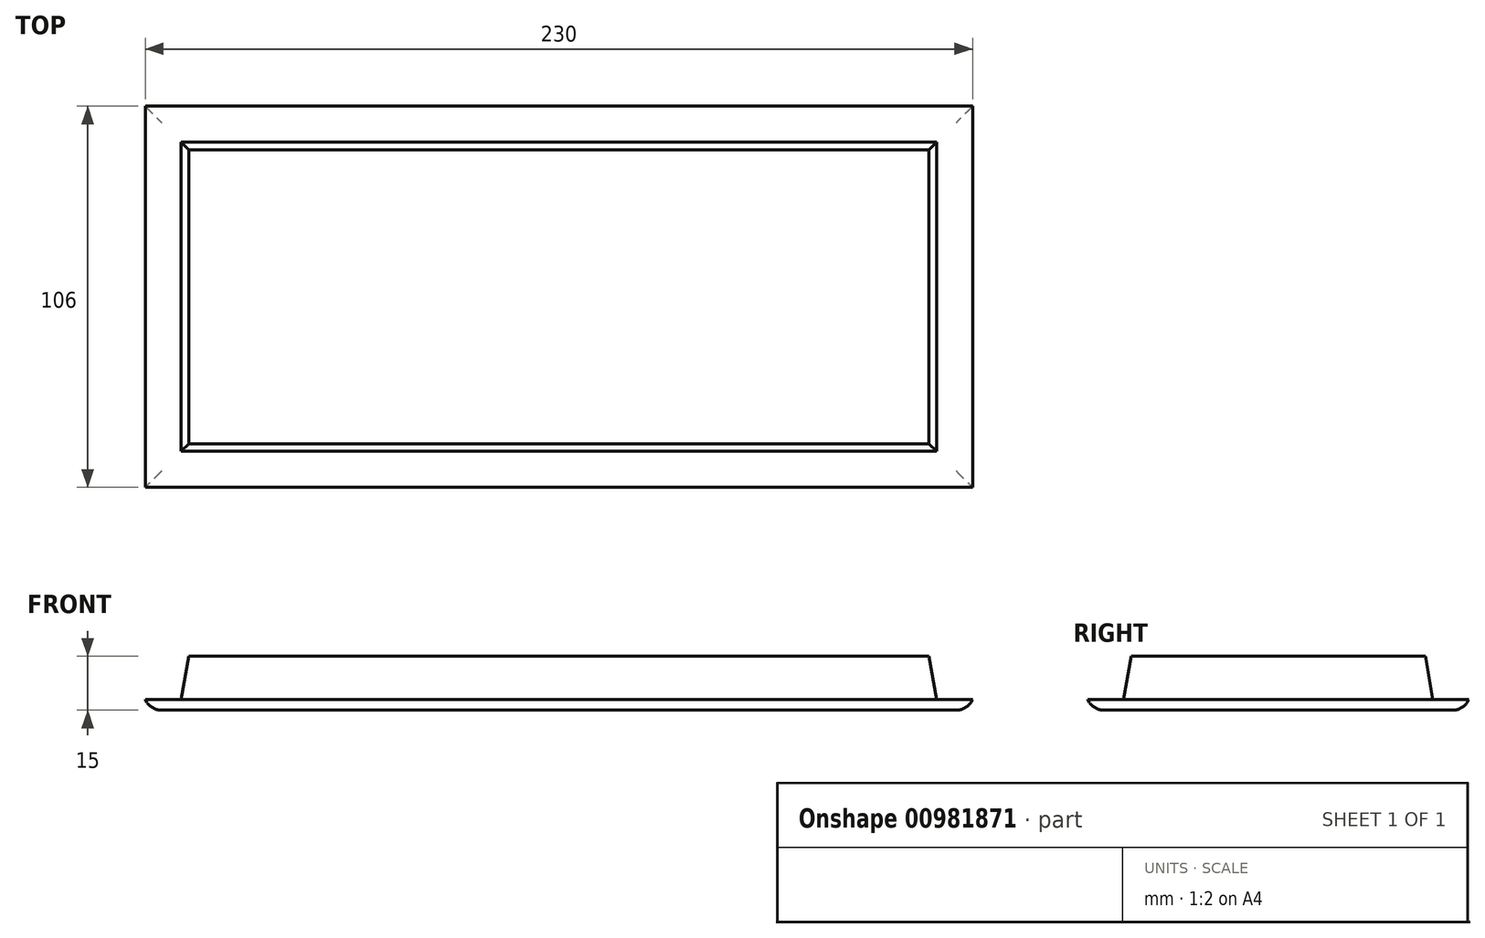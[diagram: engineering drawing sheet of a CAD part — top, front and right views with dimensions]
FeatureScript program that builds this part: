
annotation { "Feature Type Name" : "Feature", "Feature Type Description" : "" }
export const myFeature = defineFeature(function(context is Context, id is Id, definition is map)
    precondition{}
    {
        {
            var Q0;
            Q0=qCreatedBy(makeId("Top.planeOp"),FACE);
            var sketch = newSketch(context, id + "F0", { "sketchPlane" : qUnion([Q0])});
            skLineSegment(sketch, "E0.bottom", {"start": v(105, -43) * mm, "end": v(-105, -43) * mm});
            skLineSegment(sketch, "E0.top", {"start": v(105, 43) * mm, "end": v(-105, 43) * mm});
            skLineSegment(sketch, "E0.left", {"start": v(105, -43) * mm, "end": v(105, 43) * mm});
            skLineSegment(sketch, "E0.right", {"start": v(-105, -43) * mm, "end": v(-105, 43) * mm});
            skPoint(sketch, "E0.middle", {"position": v(0, 0) * mm});
            skLineSegment(sketch, "E1.bottom", {"start": v(115, -53) * mm, "end": v(-115, -53) * mm});
            skLineSegment(sketch, "E1.top", {"start": v(115, 53) * mm, "end": v(-115, 53) * mm});
            skLineSegment(sketch, "E1.left", {"start": v(115, -53) * mm, "end": v(115, 53) * mm});
            skLineSegment(sketch, "E1.right", {"start": v(-115, -53) * mm, "end": v(-115, 53) * mm});
            skSolve(sketch);
        }
        {
            var Q0;
            Q0=makeQuery(id+"F0.imprint","IMPRINT",FACE,{"disambiguationData":[TD([[makeQuery(id+"F0.imprint","IMPRINT",EDGE,{"derivedFrom":sQuery(id+"F0.wireOp",EDGE,"E0.bottom")}),-1.0]])]});
            extrude(context, id + "F1", {"entities" : qUnion([Q0]), "depth" : 15 * mm, "offsetDistance" : 25 * mm});
        }
        {
            var Q0;
            Q0=makeQuery(id+"F0.imprint","IMPRINT",FACE,{"disambiguationData":[TD([[makeQuery(id+"F0.imprint","IMPRINT",EDGE,{"derivedFrom":sQuery(id+"F0.wireOp",EDGE,"E0.bottom")}),1.0]])]});
            extrude(context, id + "F2", {"entities" : qUnion([Q0]), "operationType" : NewBodyOperationType.ADD, "depth" : 3 * mm, "offsetDistance" : 25 * mm});
        }
        {
            var Q0;
            {var subQ0=sQuery(id+"F0.wireOp",EDGE,"E0.right");var subQ1=sQuery(id+"F0.wireOp",EDGE,"E0.left");var subQ2=sQuery(id+"F0.wireOp",EDGE,"E0.top");var subQ3=sQuery(id+"F0.wireOp",EDGE,"E0.bottom");Q0=makeQuery(id+"F2.boolean.opBoolean","MERGE",FACE,{"derivedFrom":[makeQuery(id+"F1.opExtrude","CAP_FACE",FACE,{"disambiguationData":[OSD([subQ3,subQ2,subQ1,subQ0])],"isStart":true}),makeQuery(id+"F2.opExtrude","CAP_FACE",FACE,{"disambiguationData":[OSD([subQ3,subQ2,subQ1,subQ0,sQuery(id+"F0.wireOp",EDGE,"E1.bottom"),sQuery(id+"F0.wireOp",EDGE,"E1.top"),sQuery(id+"F0.wireOp",EDGE,"E1.left"),sQuery(id+"F0.wireOp",EDGE,"E1.right")])],"isStart":true})]});}
            fillet(context, id + "F3", {"entities" : qUnion([Q0]), "radius" : 5 * mm, "tangentPropagation" : true, "allowEdgeOverflow" : false});
        }
        {
            var Q0;
            Q0=makeQuery(id+"F1.opExtrude","CAP_FACE",FACE,{"disambiguationData":[OSD([sQuery(id+"F0.wireOp",EDGE,"E0.bottom"),sQuery(id+"F0.wireOp",EDGE,"E0.top"),sQuery(id+"F0.wireOp",EDGE,"E0.left"),sQuery(id+"F0.wireOp",EDGE,"E0.right")])],"isStart":false});
            chamfer(context, id + "F4", {"entities" : qUnion([Q0]), "chamferType" : ChamferType.OFFSET_ANGLE, "width" : 12 * mm, "oppositeDirection" : false, "angle" : 10 * degree, "tangentPropagation" : true});
        }
    });
